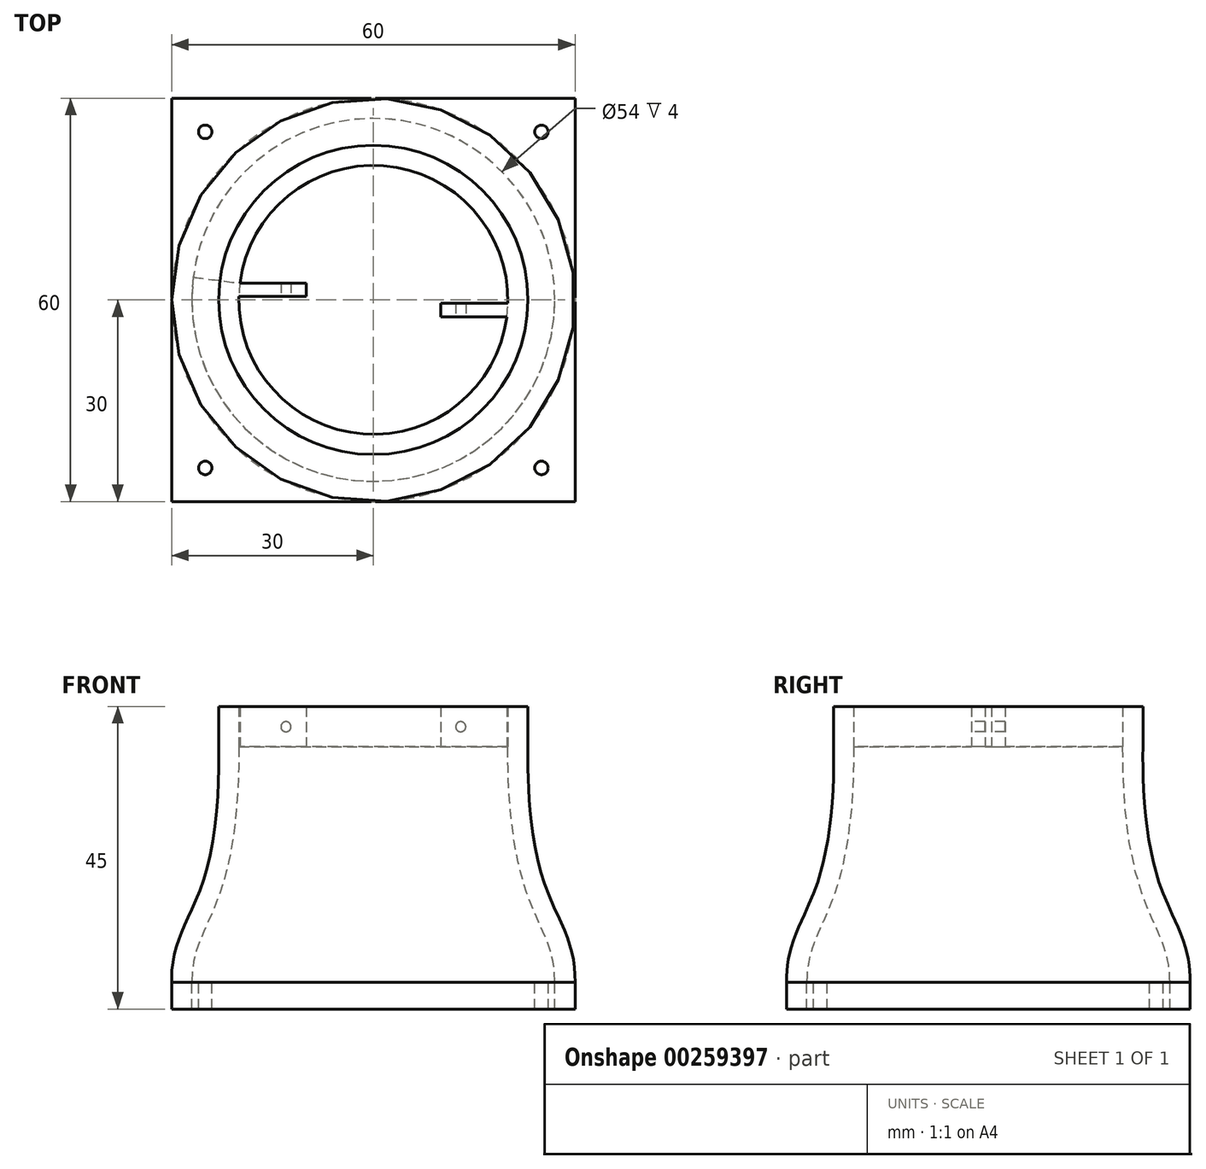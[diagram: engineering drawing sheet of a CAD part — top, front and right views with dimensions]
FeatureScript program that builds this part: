
annotation { "Feature Type Name" : "Feature", "Feature Type Description" : "" }
export const myFeature = defineFeature(function(context is Context, id is Id, definition is map)
    precondition{}
    {
        {
            var Q0;
            Q0=qCreatedBy(makeId("Top.planeOp"),FACE);
            var sketch = newSketch(context, id + "F0", { "sketchPlane" : qUnion([Q0])});
            skLineSegment(sketch, "E0.bottom", {"start": v(-30, 30) * mm, "end": v(30, 30) * mm});
            skLineSegment(sketch, "E0.top", {"start": v(-30, -30) * mm, "end": v(30, -30) * mm});
            skLineSegment(sketch, "E0.left", {"start": v(-30, 30) * mm, "end": v(-30, -30) * mm});
            skLineSegment(sketch, "E0.right", {"start": v(30, 30) * mm, "end": v(30, -30) * mm});
            skCircle(sketch, "E1", {"center": v(0, 0) * mm, "radius": 27 * mm});
            skCircle(sketch, "E2", {"center": v(-25, 25) * mm, "radius": 1 * mm});
            skCircle(sketch, "E3", {"center": v(25, 25) * mm, "radius": 1 * mm});
            skCircle(sketch, "E4", {"center": v(25, -25) * mm, "radius": 1 * mm});
            skCircle(sketch, "E5", {"center": v(-25, -25) * mm, "radius": 1 * mm});
            skSolve(sketch);
        }
        {
            var Q0;
            Q0=makeQuery(id+"F0.imprint","IMPRINT",FACE,{"disambiguationData":[TD([[makeQuery(id+"F0.imprint","IMPRINT",EDGE,{"derivedFrom":sQuery(id+"F0.wireOp",EDGE,"E0.bottom")}),-1.0]])]});
            extrude(context, id + "F1", {"entities" : qUnion([Q0]), "oppositeDirection" : true, "depth" : 4 * mm});
        }
        {
            var Q0;
            Q0=qCreatedBy(makeId("Top.planeOp"),FACE);
            cPlane(context, id + "F2", {"entities" : qUnion([Q0]), "cplaneType" : CPlaneType.OFFSET, "offset" : 35 * mm, "width" : 150 * mm, "height" : 150 * mm});
        }
        {
            var Q0;
            Q0=qCreatedBy(id+"F2.planeOp",FACE);
            var sketch = newSketch(context, id + "F3", { "sketchPlane" : qUnion([Q0])});
            skCircle(sketch, "E6", {"center": v(0, 0) * mm, "radius": 20 * mm});
            skLineSegment(sketch, "E7", {"start": v(-20, 0) * mm, "end": v(20, 0) * mm, "construction": true});
            skLineSegment(sketch, "E8", {"start": v(0, 20) * mm, "end": v(0, -20) * mm, "construction": true});
            skLineSegment(sketch, "E9", {"start": v(-20, 0.5) * mm, "end": v(-10, 0.5) * mm});
            skLineSegment(sketch, "E10", {"start": v(-10, 0.5) * mm, "end": v(-10, 2.5) * mm});
            skLineSegment(sketch, "E11", {"start": v(-10, 2.5) * mm, "end": v(-19.84, 2.5) * mm});
            skLineSegment(sketch, "E12.1.0", {"start": v(20, -0.5) * mm, "end": v(10, -0.5) * mm});
            skLineSegment(sketch, "E12.1.1", {"start": v(10, -0.5) * mm, "end": v(10, -2.5) * mm});
            skLineSegment(sketch, "E12.1.2", {"start": v(10, -2.5) * mm, "end": v(19.84, -2.5) * mm});
            skCircle(sketch, "E13", {"center": v(0, 0) * mm, "radius": 23 * mm});
            skSolve(sketch);
        }
        {
            var Q0;
            Q0=makeQuery(id+"F3.imprint","IMPRINT",FACE,{"disambiguationData":[TD([[makeQuery(id+"F3.imprint","IMPRINT",EDGE,{"derivedFrom":sQuery(id+"F3.wireOp",EDGE,"E13")}),1.0]])]});
            var Q1;
            {var subQ0=sQuery(id+"F3.wireOp",EDGE,"E9");Q1=makeQuery(id+"F3.imprint","IMPRINT",FACE,{"disambiguationData":[TD([[makeQuery(id+"F3.imprint","IMPRINT",EDGE,{"derivedFrom":subQ0}),1.0]])]});}
            var Q2;
            {var subQ0=sQuery(id+"F3.wireOp",EDGE,"E12.1.0");Q2=makeQuery(id+"F3.imprint","IMPRINT",FACE,{"disambiguationData":[TD([[makeQuery(id+"F3.imprint","IMPRINT",EDGE,{"derivedFrom":subQ0}),1.0]])]});}
            extrude(context, id + "F4", {"entities" : qUnion([Q0, Q1, Q2]), "depth" : 6 * mm});
        }
        {
            var Q0;
            Q0=qCreatedBy(makeId("Front.planeOp"),FACE);
            var sketch = newSketch(context, id + "F5", { "sketchPlane" : qUnion([Q0])});
            skLineSegment(sketch, "E14.0.0", {"start": v(-20, 35) * mm, "end": v(-10, 35) * mm, "construction": true});
            skLineSegment(sketch, "E14.0.1", {"start": v(-10, 35) * mm, "end": v(-10, 41) * mm, "construction": true});
            skLineSegment(sketch, "E14.0.2", {"start": v(-10, 41) * mm, "end": v(-20, 41) * mm, "construction": true});
            skLineSegment(sketch, "E14.0.3", {"start": v(-20, 41) * mm, "end": v(-20, 35) * mm, "construction": true});
            skLineSegment(sketch, "E14.1.0", {"start": v(20, 35) * mm, "end": v(10, 35) * mm, "construction": true});
            skLineSegment(sketch, "E14.1.1", {"start": v(10, 35) * mm, "end": v(10, 41) * mm, "construction": true});
            skLineSegment(sketch, "E14.1.2", {"start": v(10, 41) * mm, "end": v(20, 41) * mm, "construction": true});
            skLineSegment(sketch, "E14.1.3", {"start": v(20, 41) * mm, "end": v(20, 35) * mm, "construction": true});
            skPoint(sketch, "E15", {"position": v(0, 38) * mm});
            skPoint(sketch, "E16", {"position": v(-13, 38) * mm});
            skPoint(sketch, "E17", {"position": v(13, 38) * mm});
            skCircle(sketch, "E18", {"center": v(-13, 38) * mm, "radius": 0.75 * mm});
            skCircle(sketch, "E19", {"center": v(13, 38) * mm, "radius": 0.75 * mm});
            skSolve(sketch);
        }
        {
            var Q0;
            Q0 = qSketchRegion(id + "F5", true);
            extrude(context, id + "F6", {"entities" : qUnion([Q0]), "operationType" : NewBodyOperationType.REMOVE, "oppositeDirection" : true, "depth" : 5 * mm, "hasSecondDirection" : true, "secondDirectionOppositeDirection" : false, "secondDirectionDepth" : 5 * mm});
        }
        {
            var Q0;
            Q0=qCreatedBy(makeId("Right.planeOp"),FACE);
            var sketch = newSketch(context, id + "F7", { "sketchPlane" : qUnion([Q0])});
            skLineSegment(sketch, "E20", {"start": v(0, -35.46) * mm, "end": v(0, 61.95) * mm, "construction": true});
            skLineSegment(sketch, "E21.0", {"start": v(-27, 0) * mm, "end": v(27, 0) * mm, "construction": true});
            skLineSegment(sketch, "E21.1", {"start": v(-20, 35) * mm, "end": v(20, 35) * mm, "construction": true});
            skFitSpline(sketch, "E22", {"points": [v(27, 0) * mm, v(20, 35) * mm], "startDerivative": vector(0, 28.41) * mm, "endDerivative": vector(0, 76.59) * mm});
            skFitSpline(sketch, "E23.0", {"points": [v(30, 0) * mm, v(30, 0.68) * mm, v(29.94, 2) * mm, v(29.67, 3.79) * mm, v(29.25, 5.44) * mm, v(28.72, 6.95) * mm, v(28.14, 8.37) * mm, v(27.32, 10.19) * mm, v(26.28, 12.5) * mm, v(25.07, 15.85) * mm, v(24, 20.34) * mm, v(23.21, 26.45) * mm, v(23, 31.88) * mm, v(23, 35) * mm]});
            skLineSegment(sketch, "E24", {"start": v(20, 35) * mm, "end": v(23, 35) * mm});
            skLineSegment(sketch, "E25", {"start": v(27, 0) * mm, "end": v(30, 0) * mm});
            skSolve(sketch);
        }
        {
            var Q0;
            Q0 = qSketchRegion(id + "F7", true);
            var Q1;
            Q1=sQuery(id+"F7.wireOp",EDGE,"E20");
            revolve(context, id + "F8", {"operationType" : NewBodyOperationType.ADD, "entities" : qUnion([Q0]), "axis" : qUnion([Q1]), "revolveType" : RevolveType.FULL});
        }
    });
